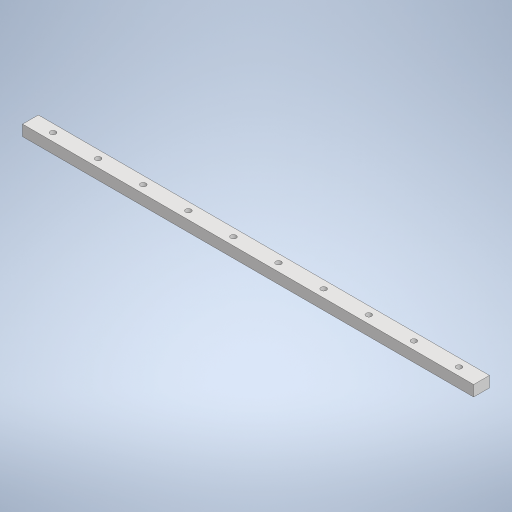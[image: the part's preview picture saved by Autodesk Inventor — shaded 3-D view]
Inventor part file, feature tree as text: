
AUTODESK INVENTOR PART (.ipt)
format: ipt  version: 2024 (Build 280153000, 153)  size: 258,560 bytes
history: native  units: mm
features: extrude x2, sketch x2
ambient origin geometry x8: Origin, YZ Plane, XZ Plane, XY Plane, X Axis, Y Axis, Z Axis, Center Point
bodies: Solid1 (feature_tree)
feature tree (4):
  extrude  "Extrusion1"  Depth=7.0mm
  extrude  "Extrusion2"  Depth=10.0mm
  sketch  "Sketch1"  dims[d0=4.8mm d1=7.0mm]
  sketch  "Sketch2"  dims[d2=200.0mm d3=0.0mm d4=2.4mm d5=10.0mm d6=3.5mm d7=100.0mm d9=20.0mm d10=10.0mm d12=10.0mm d14=0.0mm d15=0.0mm]
